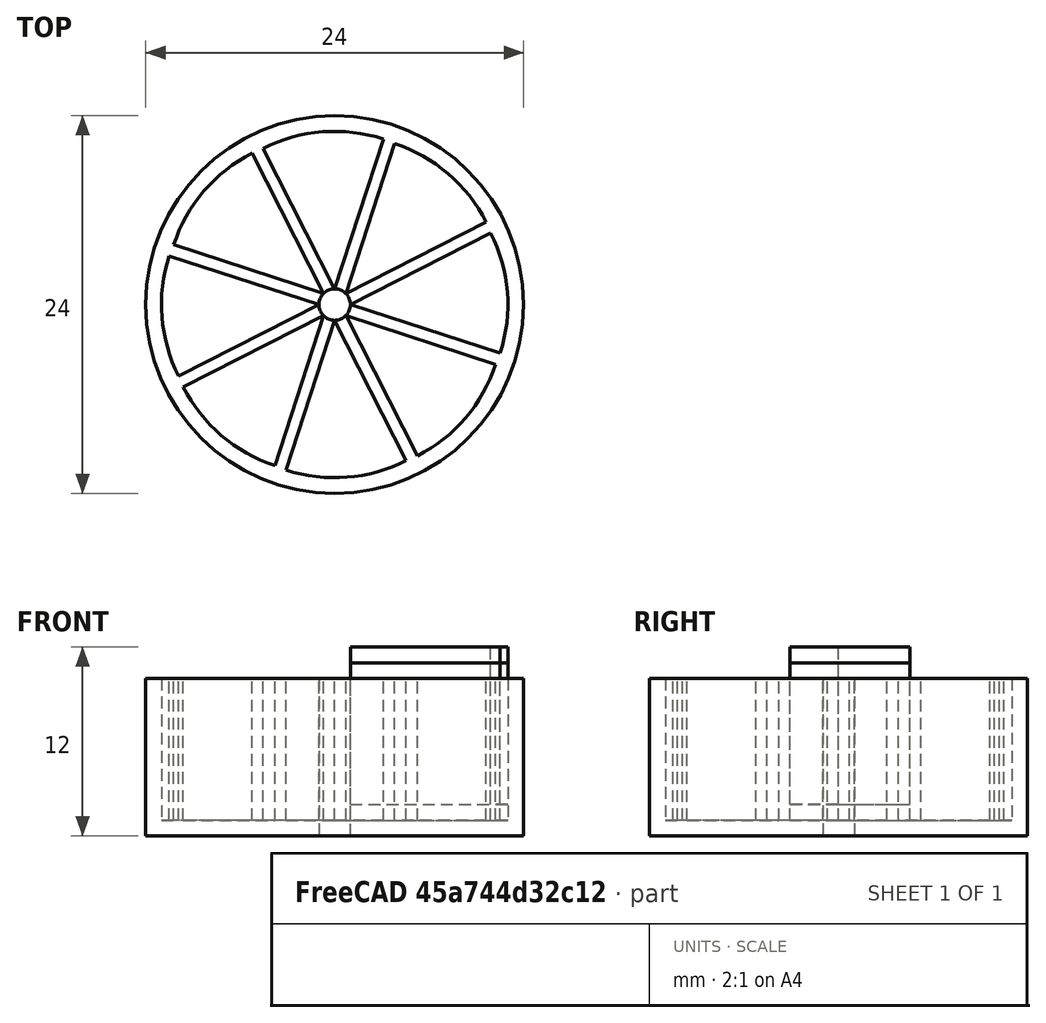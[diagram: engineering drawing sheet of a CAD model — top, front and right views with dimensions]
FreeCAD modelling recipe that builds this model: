
FCSTD DOCUMENT  (FreeCAD 0.21R33694 (Git))
Label: OJT1_T011_Trivial
License: All rights reserved
LicenseURL: https://en.wikipedia.org/wiki/All_rights_reserved
objects: Part::Cylinder×4, Part::FeaturePython×1, Part::Cut×1
note: 5 computed .brp shape members not serialized (recipe doc carries the construction recipe); baked Part::Feature solids carry a one-line shape summary decoded from their .brp

FEATURE [Part::Cylinder] Cylinder  label="Cilindre"
  Angle = 360
  AttacherType = Attacher::AttachEngine3D
  FirstAngle = 0
  Height = 10
  Radius = 12
  SecondAngle = 0
FEATURE [Part::Cylinder] Cylinder001  label="Cilindre001"
  Angle = 360
  AttacherType = Attacher::AttachEngine3D
  FirstAngle = 0
  Height = 10
  Radius = 1
  SecondAngle = 0
FEATURE [Part::Cylinder] Cylinder002  label="Cilindre002"
  Angle = 45
  AttacherType = Attacher::AttachEngine3D
  FirstAngle = 0
  Height = 10
  Placement = pos=(1,0,1) rot=(0,0,-1;0.314159rad)
  Radius = 10
  SecondAngle = 0
  expr: .Placement.Base.x = 1
FEATURE [Part::FeaturePython] Array  # Draft array (typed FeaturePython)
  AlwaysSyncPlacement = false
  Angle = 360
  ArrayType = 1
  Axis = (0,0,1)
  Base = -> Cylinder002
  Center = (0,0,0)
  Count = 8
  ExpandArray = false
  Fuse = false
  IntervalAxis = (0,0,0)
  IntervalX = (100,0,0)
  IntervalY = (0,100,0)
  IntervalZ = (0,0,100)
  NumberCircles = 3
  NumberPolar = 8
  NumberX = 2
  NumberY = 2
  NumberZ = 1
  PlacementList = 8 placements: [(1,0,1),(0.707107,0.707107,1),(0,1,1),(-0.707107,0.707107,1),(-1,1.22465e-16,1),(-0.707107,-0.707107,1),(-2.22045e-16,-1,1),(0.707107,-0.707107,1)]
  RadialDistance = 50
  ScaleList = (8) [(1,1,1),(1,1,1),(1,1,1),(1,1,1),(1,1,1),(1,1,1),(1,1,1),(1,1,1)]
  Symmetry = 1
  TangentialDistance = 25
FEATURE [Part::Cut] Cut
  Base = -> Cylinder
  Tool = -> Array
FEATURE [Part::Cylinder] Cylinder003  label="Cilindre003"
  Angle = 45
  AttacherType = Attacher::AttachEngine3D
  FirstAngle = 0
  Height = 10
  Placement = pos=(1,0,2) rot=(0,0,-1;0.314159rad)
  Radius = 10
  SecondAngle = 0
  expr: .Placement.Base.x = 1
